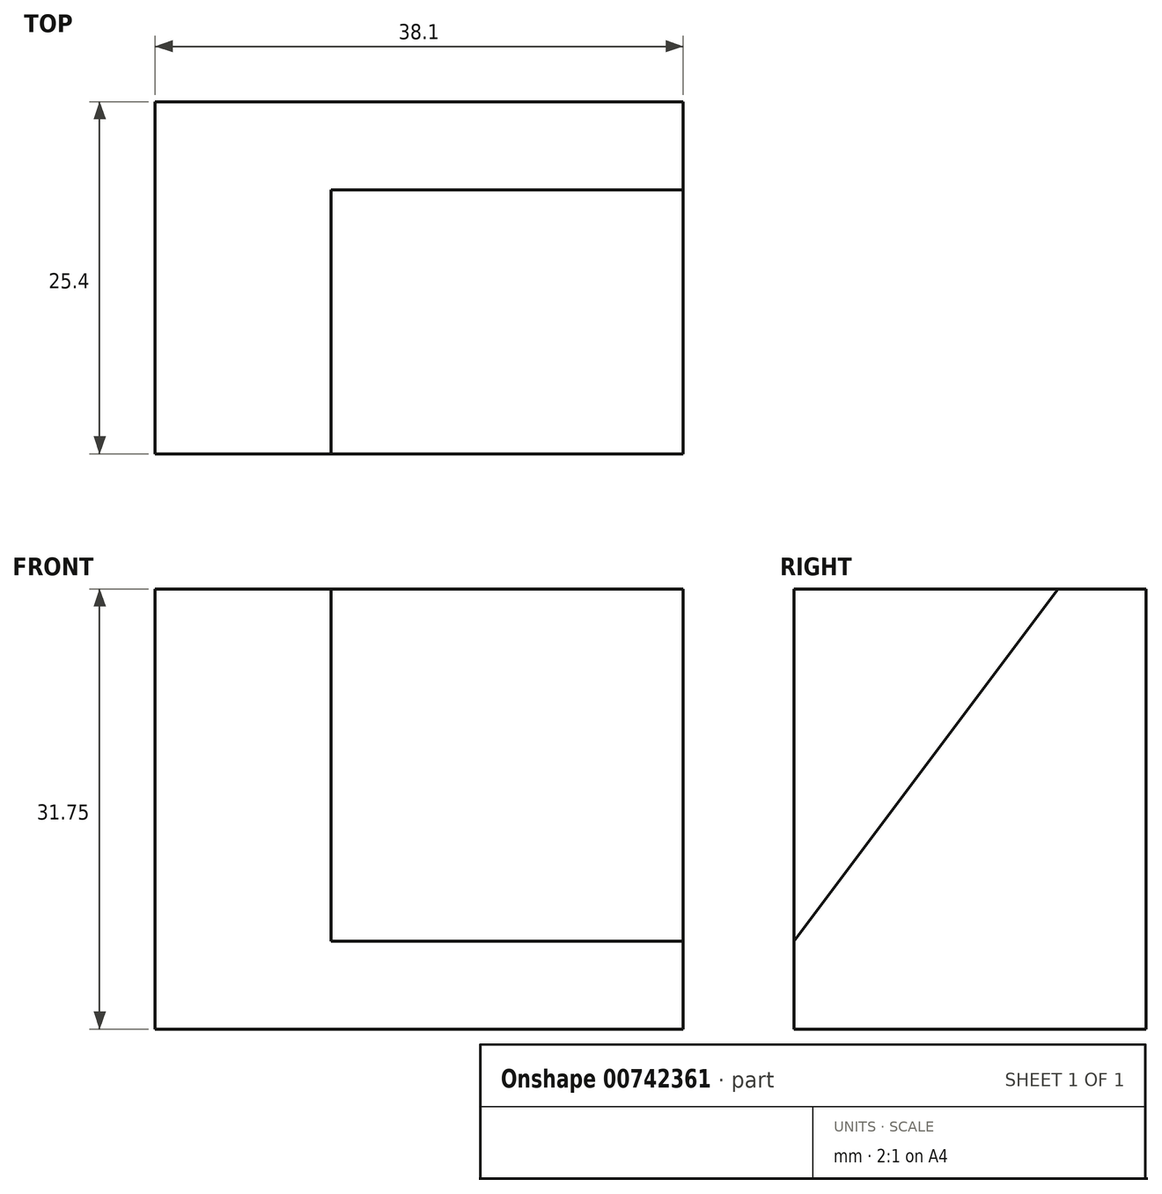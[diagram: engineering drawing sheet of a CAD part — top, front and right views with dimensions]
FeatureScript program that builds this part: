
annotation { "Feature Type Name" : "Feature", "Feature Type Description" : "" }
export const myFeature = defineFeature(function(context is Context, id is Id, definition is map)
    precondition{}
    {
        {
            var Q0;
            Q0=qCreatedBy(makeId("Front.planeOp"),FACE);
            var sketch = newSketch(context, id + "F0", { "sketchPlane" : qUnion([Q0])});
            skLineSegment(sketch, "E0", {"start": v(0, 31.75) * mm, "end": v(0, 0) * mm});
            skLineSegment(sketch, "E1", {"start": v(0, 0) * mm, "end": v(38.1, 0) * mm});
            skLineSegment(sketch, "E2", {"start": v(38.1, 0) * mm, "end": v(38.1, 31.75) * mm});
            skLineSegment(sketch, "E3", {"start": v(0, 31.75) * mm, "end": v(38.1, 31.75) * mm});
            skSolve(sketch);
        }
        {
            var Q0;
            Q0 = qSketchRegion(id + "F0", true);
            extrude(context, id + "F1", {"entities" : qUnion([Q0]), "depth" : 25.4 * mm, "offsetDistance" : 25.4 * mm});
        }
        {
            var Q0;
            Q0=makeQuery(id+"F1.opExtrude","SWEPT_FACE",FACE,{"disambiguationData":[OSD([sQuery(id+"F0.wireOp",EDGE,"E2")])]});
            var sketch = newSketch(context, id + "F2", { "sketchPlane" : qUnion([Q0])});
            skLineSegment(sketch, "E4", {"start": v(-6.35, 31.75) * mm, "end": v(-25.4, 6.35) * mm});
            skPoint(sketch, "E5", {"position": v(-25.4, 15.87) * mm});
            skLineSegment(sketch, "E6", {"start": v(-25.4, 6.35) * mm, "end": v(-25.4, 31.75) * mm});
            skLineSegment(sketch, "E7", {"start": v(-25.4, 31.75) * mm, "end": v(-6.35, 31.75) * mm});
            skSolve(sketch);
        }
        {
            var Q0;
            Q0=makeQuery(id+"F2.imprint","IMPRINT",FACE,{"disambiguationData":[TD([[makeQuery(id+"F2.imprint","IMPRINT",EDGE,{"derivedFrom":sQuery(id+"F2.wireOp",EDGE,"E4")}),-1.0]])]});
            extrude(context, id + "F3", {"entities" : qUnion([Q0]), "operationType" : NewBodyOperationType.REMOVE, "oppositeDirection" : true, "depth" : 25.4 * mm, "offsetDistance" : 25.4 * mm});
        }
    });
